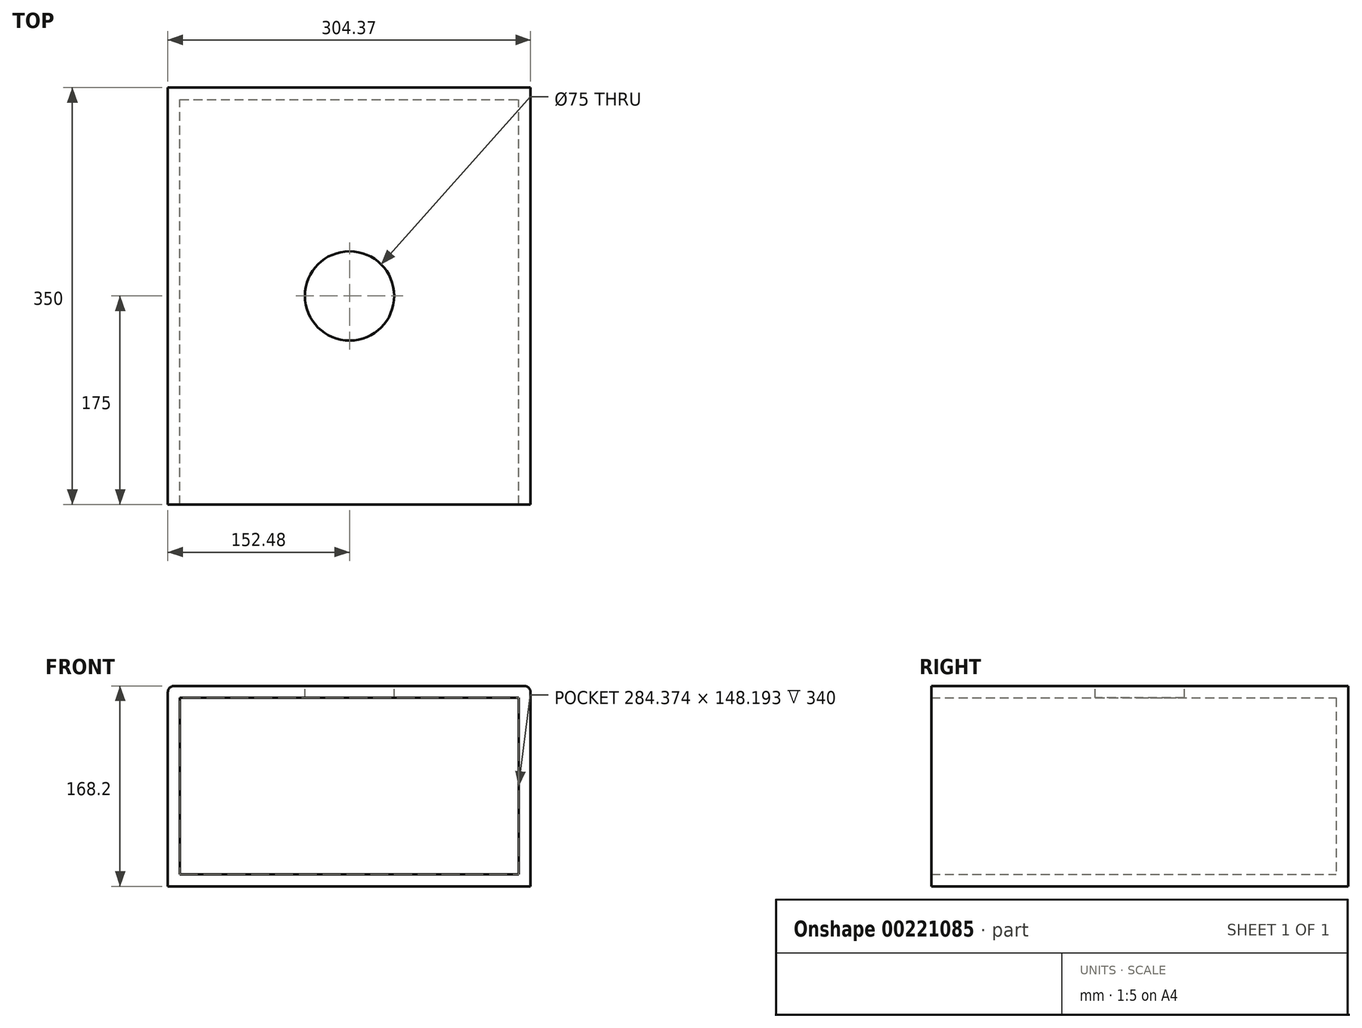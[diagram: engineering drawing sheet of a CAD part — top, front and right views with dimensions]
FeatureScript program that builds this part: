
annotation { "Feature Type Name" : "Feature", "Feature Type Description" : "" }
export const myFeature = defineFeature(function(context is Context, id is Id, definition is map)
    precondition{}
    {
        {
            var Q0;
            Q0=qCreatedBy(makeId("Front.planeOp"),FACE);
            var sketch = newSketch(context, id + "F0", { "sketchPlane" : qUnion([Q0])});
            skLineSegment(sketch, "E0.bottom", {"start": v(-152.48, 84.39) * mm, "end": v(151.9, 84.39) * mm});
            skLineSegment(sketch, "E0.top", {"start": v(-152.48, -83.8) * mm, "end": v(151.9, -83.8) * mm});
            skLineSegment(sketch, "E0.left", {"start": v(-152.48, 84.39) * mm, "end": v(-152.48, -83.8) * mm});
            skLineSegment(sketch, "E0.right", {"start": v(151.9, 84.39) * mm, "end": v(151.9, -83.8) * mm});
            skSolve(sketch);
        }
        {
            var Q0;
            Q0=makeQuery(id+"F0.imprint","IMPRINT",FACE,{"disambiguationData":[TD([[makeQuery(id+"F0.imprint","IMPRINT",EDGE,{"derivedFrom":sQuery(id+"F0.wireOp",EDGE,"E0.bottom")}),-1.0]])]});
            extrude(context, id + "F1", {"entities" : qUnion([Q0]), "endBound" : BoundingType.SYMMETRIC, "depth" : 350 * mm});
        }
        {
            var Q0;
            Q0=makeQuery(id+"F1.opExtrude","CAP_FACE",FACE,{"disambiguationData":[OSD([sQuery(id+"F0.wireOp",EDGE,"E0.bottom"),sQuery(id+"F0.wireOp",EDGE,"E0.top"),sQuery(id+"F0.wireOp",EDGE,"E0.left"),sQuery(id+"F0.wireOp",EDGE,"E0.right")])],"isStart":false});
            shell(context, id + "F2", {"entities" : qUnion([Q0]), "thickness" : 10 * mm});
        }
        {
            var Q0;
            Q0=makeQuery(id+"F1.opExtrude","SWEPT_FACE",FACE,{"disambiguationData":[OSD([sQuery(id+"F0.wireOp",EDGE,"E0.bottom")])]});
            var sketch = newSketch(context, id + "F3", { "sketchPlane" : qUnion([Q0])});
            skPoint(sketch, "E1", {"position": v(0, 0) * mm});
            skSolve(sketch);
        }
        {
            var Q0;
            Q0=sQuery(id+"F3.wireOp",VERTEX,"E1");
            var Q1;
            Q1=makeQuery(id+"F1.opExtrude","SWEPT_BODY",BODY,{"disambiguationData":[OSD([sQuery(id+"F0.wireOp",EDGE,"E0.bottom"),sQuery(id+"F0.wireOp",EDGE,"E0.top"),sQuery(id+"F0.wireOp",EDGE,"E0.left"),sQuery(id+"F0.wireOp",EDGE,"E0.right")])]});
            hole(context, id + "F4", {"style" : HoleStyle.SIMPLE, "endStyle" : HoleEndStyle.BLIND, "holeDiameter" : 75 * mm, "holeDepth" : 12 * mm, "locations" : qUnion([Q0]), "scope" : qUnion([Q1])});
        }
        {
            var Q0;
            Q0=makeQuery(id+"F1.opExtrude","SWEPT_EDGE",EDGE,{"disambiguationData":[OSD([sQuery(id+"F0.wireOp",EDGE,"E0.bottom"),sQuery(id+"F0.wireOp",EDGE,"E0.left")])]});
            var Q1;
            Q1=makeQuery(id+"F1.opExtrude","SWEPT_EDGE",EDGE,{"disambiguationData":[OSD([sQuery(id+"F0.wireOp",EDGE,"E0.bottom"),sQuery(id+"F0.wireOp",EDGE,"E0.right")])]});
            fillet(context, id + "F5", {"entities" : qUnion([Q0, Q1]), "radius" : 5 * mm, "tangentPropagation" : true, "allowEdgeOverflow" : false});
        }
    });
